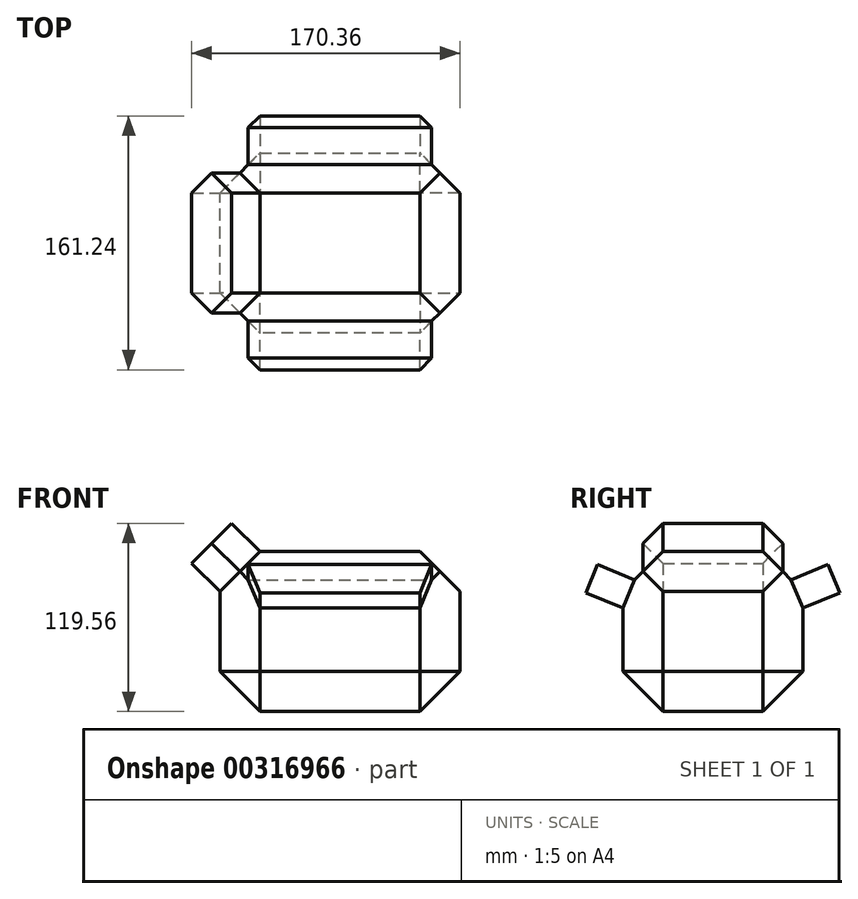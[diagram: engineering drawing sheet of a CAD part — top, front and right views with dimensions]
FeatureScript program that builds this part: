
annotation { "Feature Type Name" : "Feature", "Feature Type Description" : "" }
export const myFeature = defineFeature(function(context is Context, id is Id, definition is map)
    precondition{}
    {
        {
            var Q0;
            Q0=qCreatedBy(makeId("Top.planeOp"),FACE);
            var sketch = newSketch(context, id + "F0", { "sketchPlane" : qUnion([Q0])});
            skLineSegment(sketch, "E0.bottom", {"start": v(-77.66, 61.1) * mm, "end": v(74.74, 61.1) * mm});
            skLineSegment(sketch, "E0.top", {"start": v(-77.66, -53.2) * mm, "end": v(74.74, -53.2) * mm});
            skLineSegment(sketch, "E0.left", {"start": v(-77.66, 61.1) * mm, "end": v(-77.66, -53.2) * mm});
            skLineSegment(sketch, "E0.right", {"start": v(74.74, 61.1) * mm, "end": v(74.74, -53.2) * mm});
            skSolve(sketch);
        }
        {
            var Q0;
            Q0 = qSketchRegion(id + "F0", true);
            extrude(context, id + "F1", {"entities" : qUnion([Q0]), "depth" : 101.6 * mm});
        }
        {
            var Q0;
            Q0=makeQuery(id+"F1.opExtrude","CAP_FACE",FACE,{"disambiguationData":[OSD([sQuery(id+"F0.wireOp",EDGE,"E0.bottom"),sQuery(id+"F0.wireOp",EDGE,"E0.top"),sQuery(id+"F0.wireOp",EDGE,"E0.left"),sQuery(id+"F0.wireOp",EDGE,"E0.right")])],"isStart":false});
            chamfer(context, id + "F2", {"entities" : qUnion([Q0]), "width" : 25.4 * mm, "tangentPropagation" : true});
        }
        {
            var Q0;
            Q0=makeQuery(id+"F1.opExtrude","SWEPT_FACE",FACE,{"disambiguationData":[OSD([sQuery(id+"F0.wireOp",EDGE,"E0.top")])]});
            var Q1;
            Q1=makeQuery(id+"F1.opExtrude","SWEPT_FACE",FACE,{"disambiguationData":[OSD([sQuery(id+"F0.wireOp",EDGE,"E0.bottom")])]});
            var Q2;
            Q2=makeQuery(id+"F1.opExtrude","CAP_FACE",FACE,{"disambiguationData":[OSD([sQuery(id+"F0.wireOp",EDGE,"E0.bottom"),sQuery(id+"F0.wireOp",EDGE,"E0.top"),sQuery(id+"F0.wireOp",EDGE,"E0.left"),sQuery(id+"F0.wireOp",EDGE,"E0.right")])],"isStart":true});
            chamfer(context, id + "F3", {"entities" : qUnion([Q0, Q1, Q2]), "width" : 25.4 * mm, "tangentPropagation" : true});
        }
        {
            var Q0;
            {var subQ0=sQuery(id+"F0.wireOp",EDGE,"E0.bottom");Q0=makeQuery(id+"F3.opChamfer","BLEND_FACE",FACE,{"disambiguationData":[OSD([subQ0]),TDD([makeQuery(id+"F2.opChamfer","BLEND_EDGE",EDGE,{"blendedFrom":[makeQuery(id+"F1.opExtrude","CAP_EDGE",EDGE,{"disambiguationData":[OSD([subQ0])],"isStart":false}),makeQuery(id+"F1.opExtrude","SWEPT_FACE",FACE,{"disambiguationData":[OSD([subQ0])]})],"blendedInto":[makeQuery(id+"F1.opExtrude","SWEPT_FACE",FACE,{"disambiguationData":[OSD([subQ0])]})]})])]});}
            extrude(context, id + "F4", {"entities" : qUnion([Q0]), "operationType" : NewBodyOperationType.ADD, "depth" : 25.4 * mm});
        }
        {
            var Q0;
            {var subQ0=sQuery(id+"F0.wireOp",EDGE,"E0.top");Q0=makeQuery(id+"F3.opChamfer","BLEND_FACE",FACE,{"disambiguationData":[OSD([subQ0]),TDD([makeQuery(id+"F2.opChamfer","BLEND_EDGE",EDGE,{"blendedFrom":[makeQuery(id+"F1.opExtrude","CAP_EDGE",EDGE,{"disambiguationData":[OSD([subQ0])],"isStart":false}),makeQuery(id+"F1.opExtrude","SWEPT_FACE",FACE,{"disambiguationData":[OSD([subQ0])]})],"blendedInto":[makeQuery(id+"F1.opExtrude","SWEPT_FACE",FACE,{"disambiguationData":[OSD([subQ0])]})]})])]});}
            extrude(context, id + "F5", {"entities" : qUnion([Q0]), "operationType" : NewBodyOperationType.ADD, "depth" : 25.4 * mm});
        }
        {
            var Q0;
            Q0=makeQuery(id+"F2.opChamfer","BLEND_FACE",FACE,{"disambiguationData":[OSD([sQuery(id+"F0.wireOp",EDGE,"E0.left")])]});
            extrude(context, id + "F6", {"entities" : qUnion([Q0]), "operationType" : NewBodyOperationType.ADD, "depth" : 25.4 * mm});
        }
    });
